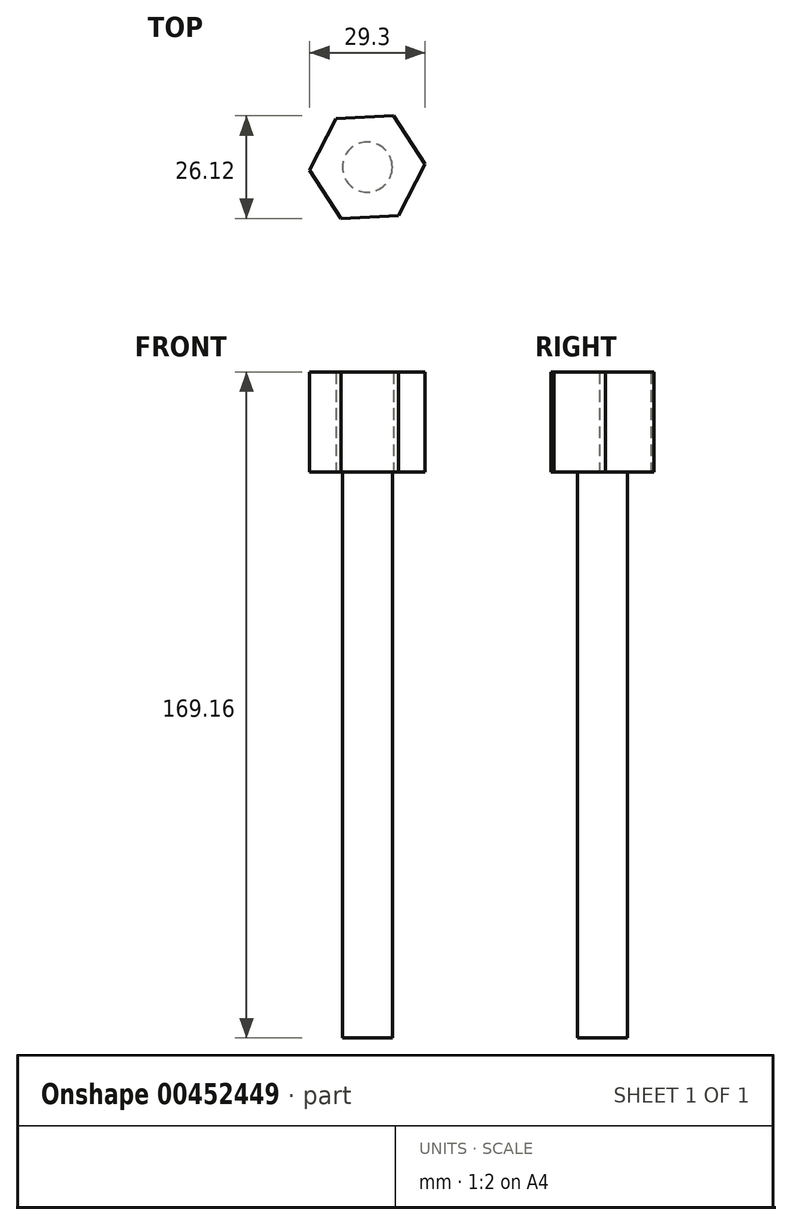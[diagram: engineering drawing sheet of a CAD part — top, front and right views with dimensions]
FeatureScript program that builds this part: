
annotation { "Feature Type Name" : "Feature", "Feature Type Description" : "" }
export const myFeature = defineFeature(function(context is Context, id is Id, definition is map)
    precondition{}
    {
        {
            var Q0;
            Q0=qCreatedBy(makeId("Top.planeOp"),FACE);
            var sketch = newSketch(context, id + "F0", { "sketchPlane" : qUnion([Q0])});
            skCircle(sketch, "E0", {"center": v(0, 0) * mm, "radius": 6.35 * mm});
            skSolve(sketch);
        }
        {
            var Q0;
            Q0 = qSketchRegion(id + "F0", true);
            extrude(context, id + "F1", {"entities" : qUnion([Q0]), "offsetDistance" : 25.4 * mm, "depth" : 76.2 * mm});
        }
        {
            var Q0;
            Q0 = qSketchRegion(id + "F0", true);
            extrude(context, id + "F2", {"entities" : qUnion([Q0]), "operationType" : NewBodyOperationType.ADD, "oppositeDirection" : true, "depth" : 67.56 * mm});
        }
        {
            var Q0;
            Q0=makeQuery(id+"F1.opExtrude","CAP_FACE",FACE,{"disambiguationData":[OSD([sQuery(id+"F0.wireOp",EDGE,"E0")])],"isStart":false});
            var sketch = newSketch(context, id + "F3", { "sketchPlane" : qUnion([Q0])});
            skCircle(sketch, "E1.cCircle", {"center": v(0, 0) * mm, "radius": 12.7 * mm, "construction": true});
            skLineSegment(sketch, "E1.0", {"start": v(6.68, 13.06) * mm, "end": v(14.65, 0.75) * mm});
            skLineSegment(sketch, "E1.1", {"start": v(14.65, 0.75) * mm, "end": v(7.97, -12.3) * mm});
            skLineSegment(sketch, "E1.2", {"start": v(7.97, -12.3) * mm, "end": v(-6.68, -13.06) * mm});
            skLineSegment(sketch, "E1.3", {"start": v(-6.68, -13.06) * mm, "end": v(-14.65, -0.75) * mm});
            skLineSegment(sketch, "E1.4", {"start": v(-14.65, -0.75) * mm, "end": v(-7.97, 12.3) * mm});
            skLineSegment(sketch, "E1.5", {"start": v(-7.97, 12.3) * mm, "end": v(6.68, 13.06) * mm});
            skPoint(sketch, "E1.0.midPoint", {"position": v(10.66, 6.9) * mm});
            skSolve(sketch);
        }
        {
            var Q0;
            Q0 = qSketchRegion(id + "F3", true);
            extrude(context, id + "F4", {"entities" : qUnion([Q0]), "operationType" : NewBodyOperationType.ADD, "depth" : 25.4 * mm});
        }
    });
